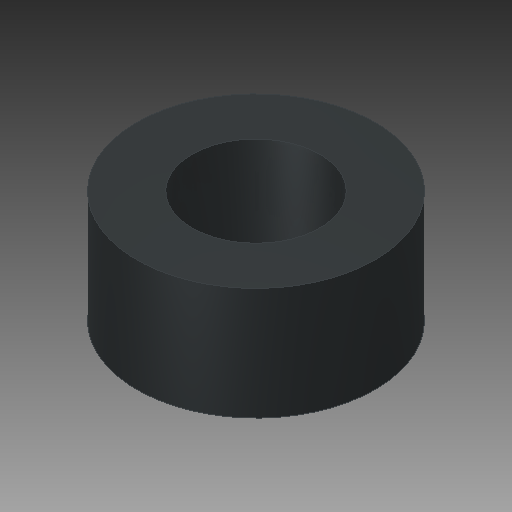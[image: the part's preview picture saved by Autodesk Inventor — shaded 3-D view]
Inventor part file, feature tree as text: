
AUTODESK INVENTOR PART (.ipt)
format: ipt  version: 2019 (Build 230136000, 136)  size: 99,840 bytes
history: native  units: mm
features: other x1, extrude x1, sketch x1
ambient origin geometry x8: Origin, YZ Plane, XZ Plane, XY Plane, X Axis, Y Axis, Z Axis, Center Point
bodies: Body1 (feature_tree)
feature tree (3):
  other  "Bryła1"
  extrude  "Wyciągnięcie proste1"  Depth=28.0mm
  sketch  "Szkic1"
